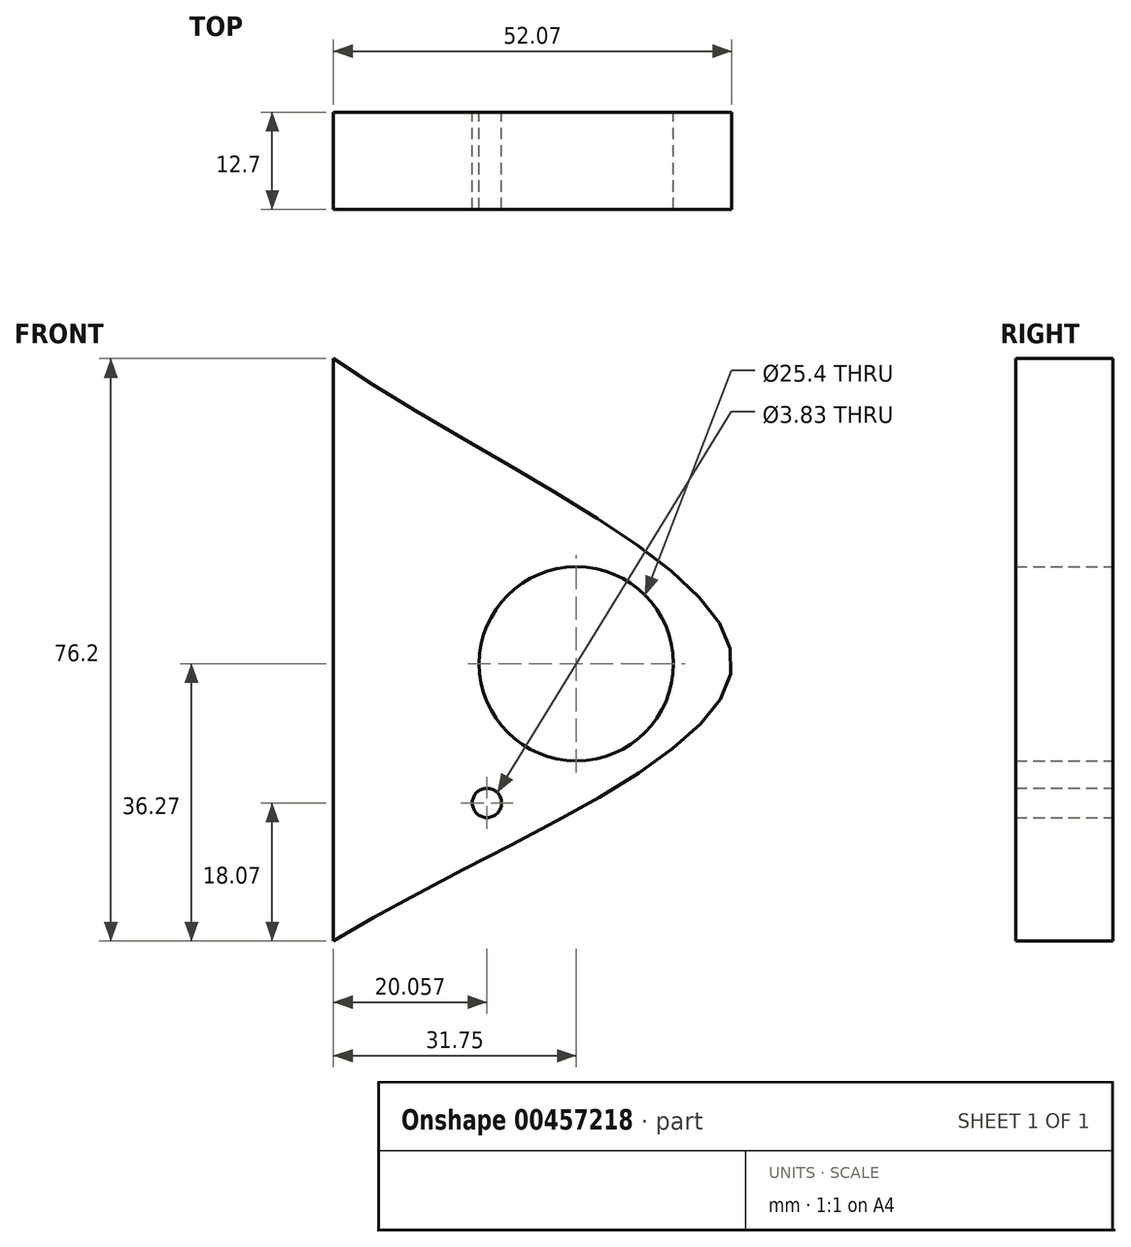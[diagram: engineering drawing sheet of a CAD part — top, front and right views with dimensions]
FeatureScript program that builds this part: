
annotation { "Feature Type Name" : "Feature", "Feature Type Description" : "" }
export const myFeature = defineFeature(function(context is Context, id is Id, definition is map)
    precondition{}
    {
        {
            var Q0;
            Q0=qCreatedBy(makeId("Front.planeOp"),FACE);
            var sketch = newSketch(context, id + "F0", { "sketchPlane" : qUnion([Q0])});
            skLineSegment(sketch, "E0", {"start": v(-52.07, 39.93) * mm, "end": v(-52.07, -36.27) * mm});
            skFitSpline(sketch, "E1", {"points": [v(-52.07, 39.93) * mm, v(0, 0) * mm, v(-52.07, -36.27) * mm], "startDerivative": vector(115.06, -80.33) * mm, "endDerivative": vector(-115.98, -72.04) * mm});
            skCircle(sketch, "E2", {"center": v(-20.32, 0) * mm, "radius": 12.7 * mm});
            skCircle(sketch, "E3", {"center": v(-32.01, -18.2) * mm, "radius": 1.91 * mm});
            skSolve(sketch);
        }
        {
            var Q0;
            Q0=makeQuery(id+"F0.imprint","IMPRINT",FACE,{"disambiguationData":[TD([[makeQuery(id+"F0.imprint","IMPRINT",EDGE,{"derivedFrom":sQuery(id+"F0.wireOp",EDGE,"E0")}),1.0]])]});
            extrude(context, id + "F1", {"entities" : qUnion([Q0]), "depth" : 25.4 * mm, "symmetric" : true});
        }
        {
            var Q0;
            Q0 = qSketchRegion(id + "F0", true);
            extrude(context, id + "F2", {"entities" : qUnion([Q0]), "operationType" : NewBodyOperationType.REMOVE, "oppositeDirection" : true, "depth" : 25.4 * mm});
        }
        {
            var Q0;
            Q0=sQuery(id+"F0.wireOp",EDGE,"E3");
            extrude(context, id + "F3", {"bodyType" : ExtendedToolBodyType.SURFACE, "surfaceEntities" : qUnion([Q0]), "depth" : 16.26 * mm});
        }
    });
